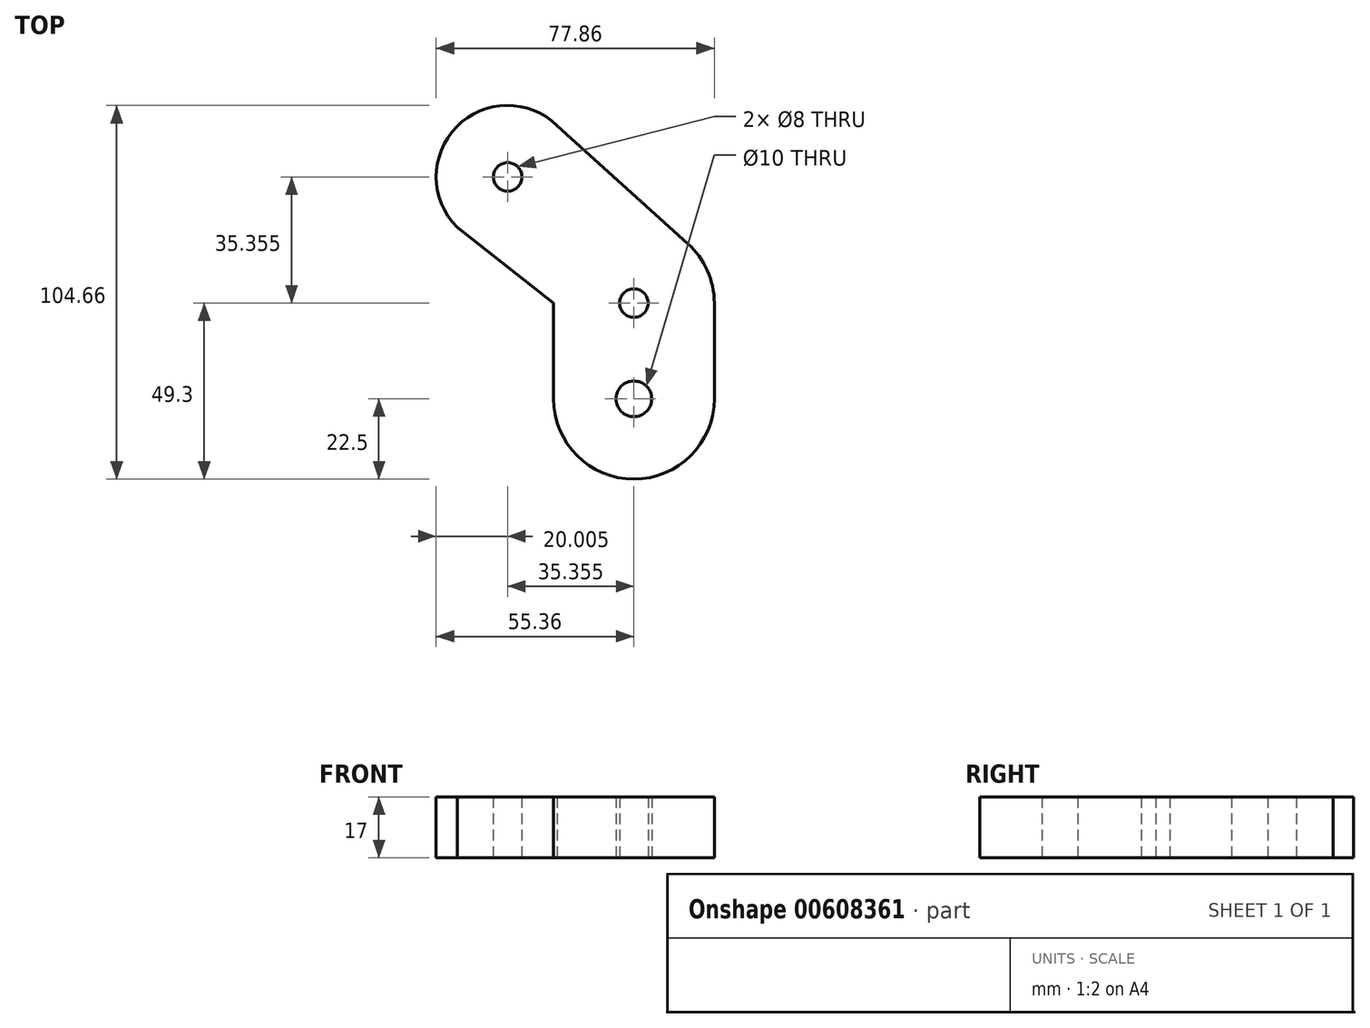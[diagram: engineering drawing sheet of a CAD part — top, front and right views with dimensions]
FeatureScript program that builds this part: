
annotation { "Feature Type Name" : "Feature", "Feature Type Description" : "" }
export const myFeature = defineFeature(function(context is Context, id is Id, definition is map)
    precondition{}
    {
        {
            var Q0;
            Q0=qCreatedBy(makeId("Top.planeOp"),FACE);
            var sketch = newSketch(context, id + "F0", { "sketchPlane" : qUnion([Q0])});
            skCircle(sketch, "E0", {"center": v(0, 0) * mm, "radius": 4 * mm});
            skCircle(sketch, "E1", {"center": v(0, -26.8) * mm, "radius": 5 * mm});
            skLineSegment(sketch, "E2", {"start": v(0, -26.8) * mm, "end": v(0, 0) * mm, "construction": true});
            skLineSegment(sketch, "E3", {"start": v(0, 0) * mm, "end": v(-35.36, 35.36) * mm, "construction": true});
            skCircle(sketch, "E4", {"center": v(-35.36, 35.36) * mm, "radius": 4 * mm});
            skArc(sketch, "E5.0", {"start": v(-21.21, 49.5) * mm, "mid": v(-51.08, 47.71) * mm, "end": v(-45.75, 18.27) * mm});
            skArc(sketch, "E6", {"start": v(22.5, 0) * mm, "mid": v(20.56, 9.13) * mm, "end": v(15.1, 16.69) * mm});
            skArc(sketch, "E7", {"start": v(-22.5, -26.8) * mm, "mid": v(0, -49.3) * mm, "end": v(22.5, -26.8) * mm});
            skLineSegment(sketch, "E8", {"start": v(-21.44, 49.72) * mm, "end": v(15.1, 16.69) * mm});
            skLineSegment(sketch, "E9", {"start": v(-38.97, -26.8) * mm, "end": v(-20.61, -26.8) * mm, "construction": true});
            skLineSegment(sketch, "E10", {"start": v(-32.97, 0) * mm, "end": v(44.7, 0) * mm, "construction": true});
            skLineSegment(sketch, "E11", {"start": v(-64.2, 6.51) * mm, "end": v(2.98, 73.7) * mm, "construction": true});
            skLineSegment(sketch, "E12", {"start": v(-22.5, 0) * mm, "end": v(-22.5, -26.8) * mm});
            skLineSegment(sketch, "E13", {"start": v(-49.5, 21.21) * mm, "end": v(-22.5, 0) * mm});
            skLineSegment(sketch, "E14", {"start": v(22.5, 0) * mm, "end": v(22.5, -26.8) * mm});
            skSolve(sketch);
        }
        {
            var Q0;
            Q0=makeQuery(id+"F0.imprint","IMPRINT",FACE,{"disambiguationData":[TD([[makeQuery(id+"F0.imprint","IMPRINT",EDGE,{"derivedFrom":sQuery(id+"F0.wireOp",EDGE,"E0")}),-1.0]])]});
            extrude(context, id + "F1", {"entities" : qUnion([Q0]), "endBound" : BoundingType.SYMMETRIC, "depth" : 17 * mm, "offsetDistance" : 25 * mm});
        }
    });
